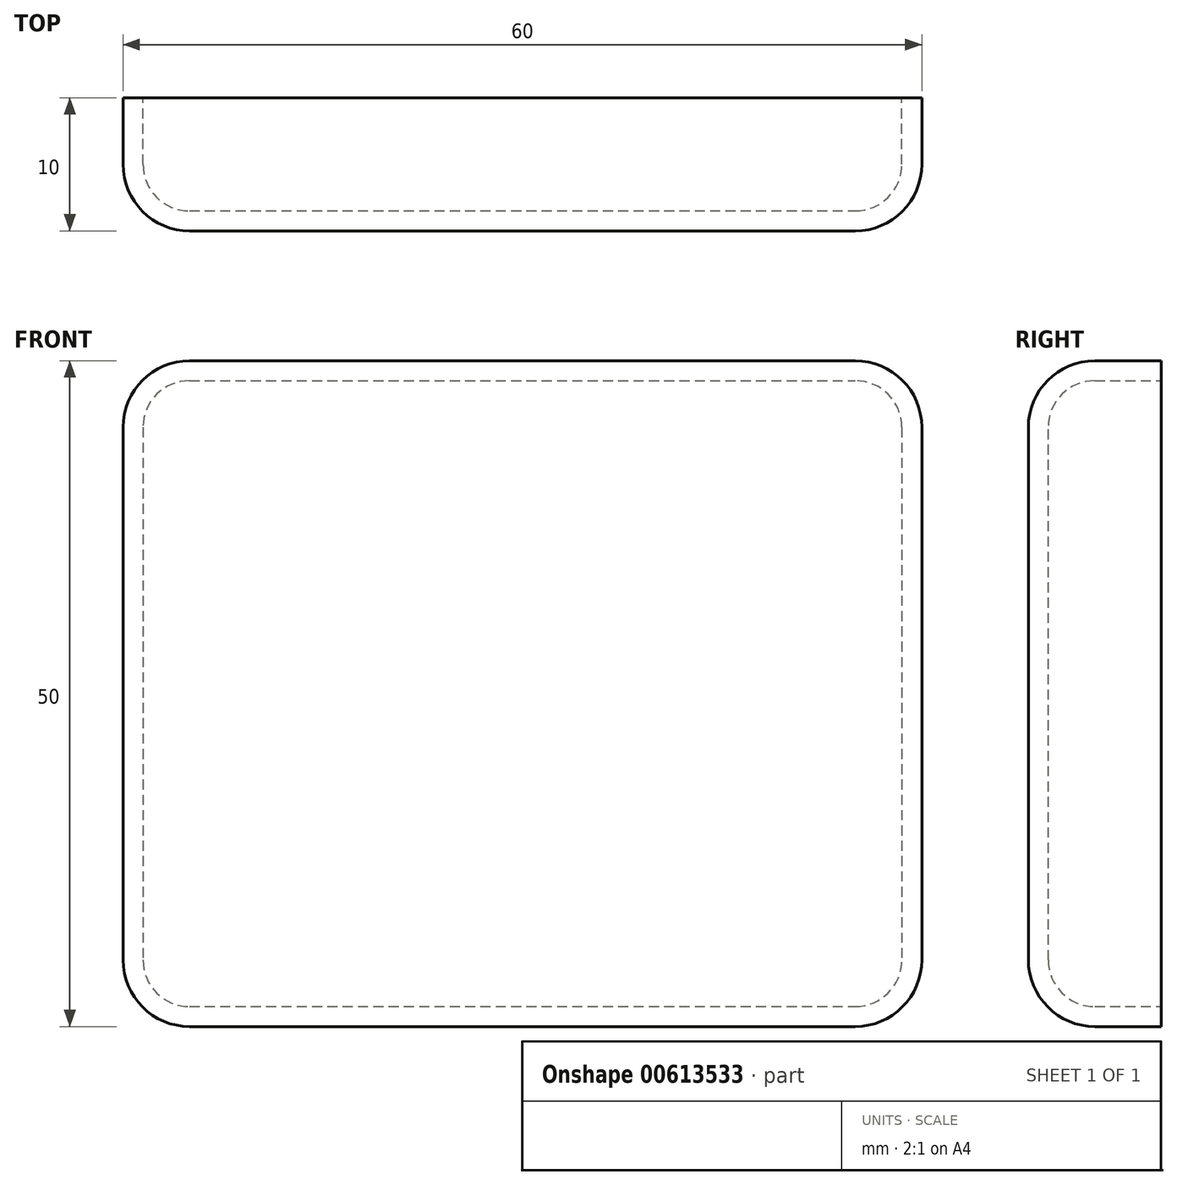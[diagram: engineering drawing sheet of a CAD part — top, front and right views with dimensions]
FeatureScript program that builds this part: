
annotation { "Feature Type Name" : "Feature", "Feature Type Description" : "" }
export const myFeature = defineFeature(function(context is Context, id is Id, definition is map)
    precondition{}
    {
        {
            var Q0;
            Q0=qCreatedBy(makeId("Front.planeOp"),FACE);
            var sketch = newSketch(context, id + "F0", { "sketchPlane" : qUnion([Q0])});
            skLineSegment(sketch, "E0.bottom", {"start": v(-60, 50) * mm, "end": v(0, 50) * mm});
            skLineSegment(sketch, "E0.top", {"start": v(-60, 0) * mm, "end": v(0, 0) * mm});
            skLineSegment(sketch, "E0.left", {"start": v(-60, 50) * mm, "end": v(-60, 0) * mm});
            skLineSegment(sketch, "E0.right", {"start": v(0, 50) * mm, "end": v(0, 0) * mm});
            skSolve(sketch);
        }
        {
            var Q0;
            Q0 = qSketchRegion(id + "F0", true);
            extrude(context, id + "F1", {"entities" : qUnion([Q0]), "depth" : 10 * mm, "offsetDistance" : 25 * mm});
        }
        {
            var Q0;
            Q0=makeQuery(id+"F1.opExtrude","SWEPT_EDGE",EDGE,{"disambiguationData":[OSD([sQuery(id+"F0.wireOp",EDGE,"E0.bottom"),sQuery(id+"F0.wireOp",EDGE,"E0.left")])]});
            var Q1;
            Q1=makeQuery(id+"F1.opExtrude","CAP_EDGE",EDGE,{"disambiguationData":[OSD([sQuery(id+"F0.wireOp",EDGE,"E0.bottom")])],"isStart":false});
            var Q2;
            Q2=makeQuery(id+"F1.opExtrude","CAP_EDGE",EDGE,{"disambiguationData":[OSD([sQuery(id+"F0.wireOp",EDGE,"E0.left")])],"isStart":false});
            var Q3;
            Q3=makeQuery(id+"F1.opExtrude","CAP_EDGE",EDGE,{"disambiguationData":[OSD([sQuery(id+"F0.wireOp",EDGE,"E0.top")])],"isStart":false});
            var Q4;
            Q4=makeQuery(id+"F1.opExtrude","CAP_EDGE",EDGE,{"disambiguationData":[OSD([sQuery(id+"F0.wireOp",EDGE,"E0.right")])],"isStart":false});
            var Q5;
            Q5=makeQuery(id+"F1.opExtrude","SWEPT_EDGE",EDGE,{"disambiguationData":[OSD([sQuery(id+"F0.wireOp",EDGE,"E0.bottom"),sQuery(id+"F0.wireOp",EDGE,"E0.right")])]});
            var Q6;
            Q6=makeQuery(id+"F1.opExtrude","SWEPT_EDGE",EDGE,{"disambiguationData":[OSD([sQuery(id+"F0.wireOp",EDGE,"E0.top"),sQuery(id+"F0.wireOp",EDGE,"E0.left")])]});
            var Q7;
            Q7=makeQuery(id+"F1.opExtrude","SWEPT_EDGE",EDGE,{"disambiguationData":[OSD([sQuery(id+"F0.wireOp",EDGE,"E0.top"),sQuery(id+"F0.wireOp",EDGE,"E0.right")])]});
            fillet(context, id + "F2", {"entities" : qUnion([Q0, Q1, Q2, Q3, Q4, Q5, Q6, Q7]), "radius" : 5 * mm, "tangentPropagation" : true, "allowEdgeOverflow" : false});
        }
        {
            var Q0;
            Q0=makeQuery(id+"F1.opExtrude","CAP_FACE",FACE,{"disambiguationData":[OSD([sQuery(id+"F0.wireOp",EDGE,"E0.bottom"),sQuery(id+"F0.wireOp",EDGE,"E0.top"),sQuery(id+"F0.wireOp",EDGE,"E0.left"),sQuery(id+"F0.wireOp",EDGE,"E0.right")])],"isStart":true});
            shell(context, id + "F3", {"entities" : qUnion([Q0]), "thickness" : 1.5 * mm});
        }
    });
